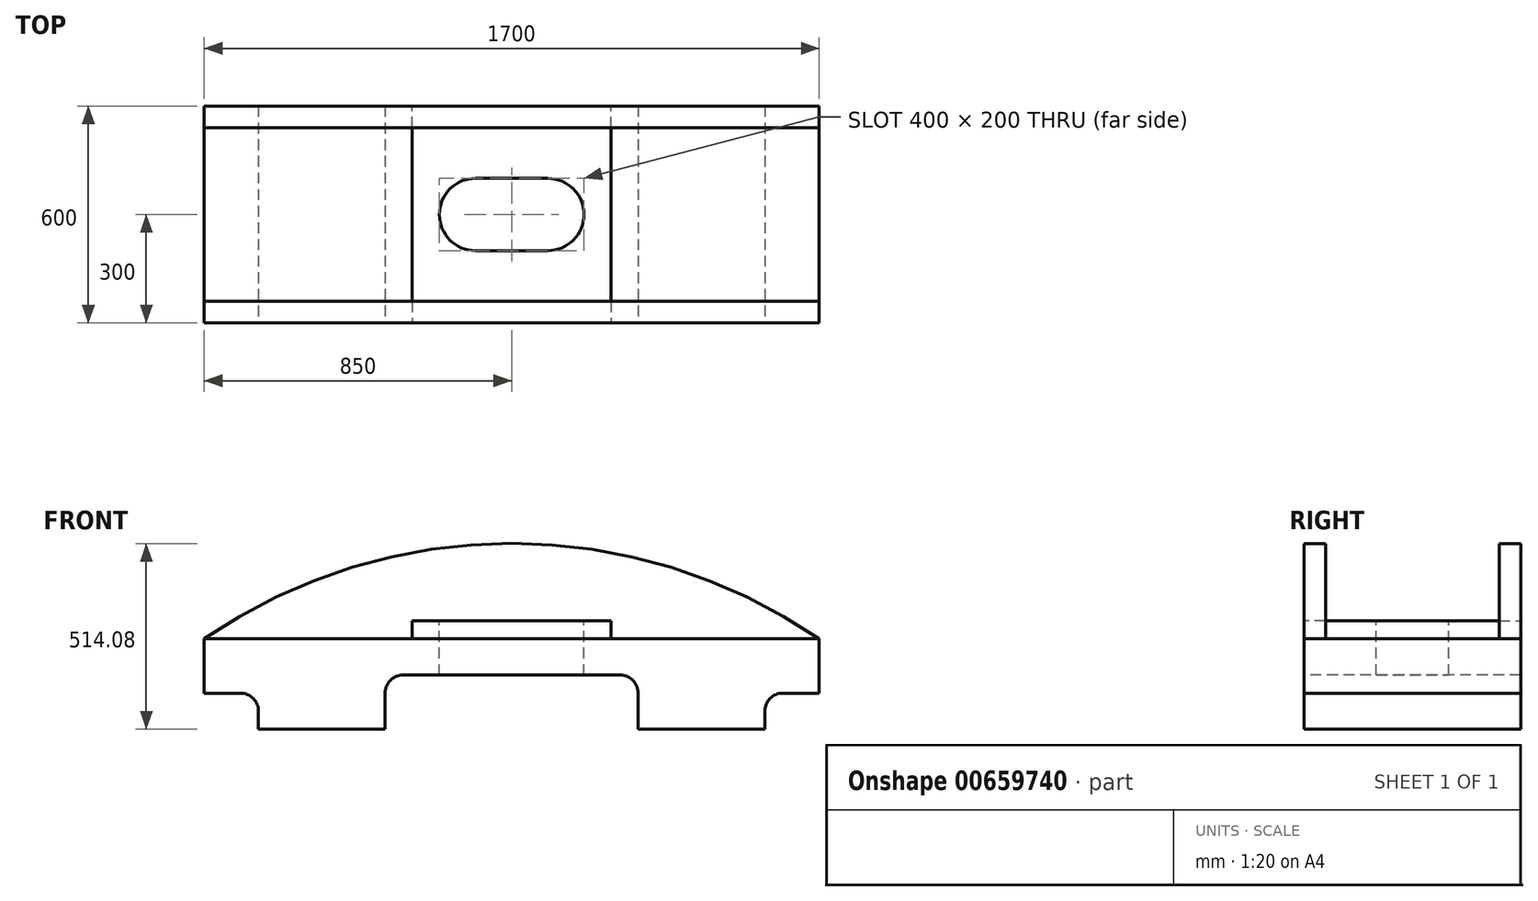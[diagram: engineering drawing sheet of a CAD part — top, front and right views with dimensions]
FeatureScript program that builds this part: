
annotation { "Feature Type Name" : "Feature", "Feature Type Description" : "" }
export const myFeature = defineFeature(function(context is Context, id is Id, definition is map)
    precondition{}
    {
        {
            var Q0;
            Q0=qCreatedBy(makeId("Front.planeOp"),FACE);
            var sketch = newSketch(context, id + "F0", { "sketchPlane" : qUnion([Q0])});
            skLineSegment(sketch, "E0.bottom", {"start": v(850, 125) * mm, "end": v(-850, 125) * mm});
            skLineSegment(sketch, "E0.top", {"start": v(850, -125) * mm, "end": v(-850, -125) * mm});
            skLineSegment(sketch, "E0.left", {"start": v(850, 125) * mm, "end": v(850, -125) * mm});
            skLineSegment(sketch, "E0.right", {"start": v(-850, 125) * mm, "end": v(-850, -125) * mm});
            skPoint(sketch, "E0.middle", {"position": v(0, 0) * mm});
            skSolve(sketch);
        }
        {
            var Q0;
            Q0 = qSketchRegion(id + "F0", true);
            extrude(context, id + "F1", {"entities" : qUnion([Q0]), "depth" : 600 * mm, "offsetDistance" : 25 * mm});
        }
        {
            var Q0;
            Q0=makeQuery(id+"F1.opExtrude","CAP_FACE",FACE,{"disambiguationData":[OSD([sQuery(id+"F0.wireOp",EDGE,"E0.bottom"),sQuery(id+"F0.wireOp",EDGE,"E0.top"),sQuery(id+"F0.wireOp",EDGE,"E0.left"),sQuery(id+"F0.wireOp",EDGE,"E0.right")])],"isStart":false});
            var sketch = newSketch(context, id + "F2", { "sketchPlane" : qUnion([Q0])});
            skPoint(sketch, "E1", {"position": v(-850, -25) * mm});
            skPoint(sketch, "E2", {"position": v(-700, -125) * mm});
            skPoint(sketch, "E3", {"position": v(850, -25) * mm});
            skPoint(sketch, "E4", {"position": v(700, -125) * mm});
            skLineSegment(sketch, "E5", {"start": v(-700, -75) * mm, "end": v(-700, -125) * mm});
            skLineSegment(sketch, "E6", {"start": v(-850, -25) * mm, "end": v(-750, -25) * mm});
            skPoint(sketch, "E7.visualSharp", {"position": v(-700, -25) * mm});
            skArc(sketch, "E7.filletArc", {"start": v(-700, -75) * mm, "mid": v(-714.64, -39.64) * mm, "end": v(-750, -25) * mm});
            skLineSegment(sketch, "E8", {"start": v(850, -25) * mm, "end": v(750, -25) * mm});
            skLineSegment(sketch, "E9", {"start": v(700, -75) * mm, "end": v(700, -125) * mm});
            skPoint(sketch, "E10.visualSharp", {"position": v(700, -25) * mm});
            skArc(sketch, "E10.filletArc", {"start": v(750, -25) * mm, "mid": v(714.64, -39.64) * mm, "end": v(700, -75) * mm});
            skLineSegment(sketch, "E11.bottom", {"start": v(300, 25) * mm, "end": v(-300, 25) * mm});
            skLineSegment(sketch, "E11.left", {"start": v(350, -25) * mm, "end": v(350, -125) * mm});
            skLineSegment(sketch, "E11.right", {"start": v(-350, -25) * mm, "end": v(-350, -125) * mm});
            skPoint(sketch, "E11.middle", {"position": v(0, -125) * mm});
            skLineSegment(sketch, "E12", {"start": v(-350, -125) * mm, "end": v(350, -125) * mm});
            skPoint(sketch, "E13.orphan", {"position": v(-350, -275) * mm});
            skPoint(sketch, "E14.orphan", {"position": v(350, -275) * mm});
            skPoint(sketch, "E15.visualSharp", {"position": v(-350, 25) * mm});
            skArc(sketch, "E15.filletArc", {"start": v(-300, 25) * mm, "mid": v(-335.36, 10.36) * mm, "end": v(-350, -25) * mm});
            skPoint(sketch, "E16.visualSharp", {"position": v(350, 25) * mm});
            skArc(sketch, "E16.filletArc", {"start": v(350, -25) * mm, "mid": v(335.36, 10.36) * mm, "end": v(300, 25) * mm});
            skSolve(sketch);
        }
        {
            var Q0;
            Q0 = qSketchRegion(id + "F2", true);
            var Q1;
            {var subQ3=sQuery(id+"F2.wireOp",EDGE,"E5");Q1=makeQuery(id+"F2.imprint","IMPRINT",FACE,{"disambiguationData":[TD([[makeQuery(id+"F2.imprint","IMPRINT",EDGE,{"derivedFrom":subQ3}),-1.0]])]});}
            var Q2;
            {var subQ4=sQuery(id+"F2.wireOp",EDGE,"E8");Q2=makeQuery(id+"F2.imprint","IMPRINT",FACE,{"disambiguationData":[TD([[makeQuery(id+"F2.imprint","IMPRINT",EDGE,{"derivedFrom":subQ4}),1.0]])]});}
            extrude(context, id + "F3", {"entities" : qUnion([Q0, Q1, Q2]), "operationType" : NewBodyOperationType.REMOVE, "endBound" : BoundingType.THROUGH_ALL, "oppositeDirection" : true, "depth" : 25 * mm, "offsetDistance" : 25 * mm});
        }
        {
            var Q0;
            Q0=makeQuery(id+"F1.opExtrude","CAP_FACE",FACE,{"disambiguationData":[OSD([sQuery(id+"F0.wireOp",EDGE,"E0.bottom"),sQuery(id+"F0.wireOp",EDGE,"E0.top"),sQuery(id+"F0.wireOp",EDGE,"E0.left"),sQuery(id+"F0.wireOp",EDGE,"E0.right")])],"isStart":false});
            var sketch = newSketch(context, id + "F4", { "sketchPlane" : qUnion([Q0])});
            skLineSegment(sketch, "E17.bottom", {"start": v(275, 175) * mm, "end": v(-275, 175) * mm});
            skLineSegment(sketch, "E17.left", {"start": v(275, 175) * mm, "end": v(275, 125) * mm});
            skLineSegment(sketch, "E17.right", {"start": v(-275, 175) * mm, "end": v(-275, 125) * mm});
            skPoint(sketch, "E17.middle", {"position": v(0, 125) * mm});
            skLineSegment(sketch, "E18", {"start": v(-275, 125) * mm, "end": v(275, 125) * mm});
            skPoint(sketch, "E19.orphan", {"position": v(-275, 75) * mm});
            skPoint(sketch, "E20.orphan", {"position": v(275, 75) * mm});
            skSolve(sketch);
        }
        {
            var Q0;
            Q0 = qSketchRegion(id + "F4", true);
            extrude(context, id + "F5", {"entities" : qUnion([Q0]), "operationType" : NewBodyOperationType.ADD, "oppositeDirection" : true, "depth" : 600 * mm, "offsetDistance" : 25 * mm});
        }
        {
            var Q0;
            Q0=makeQuery(id+"F5.opExtrude","SWEPT_FACE",FACE,{"disambiguationData":[OSD([sQuery(id+"F4.wireOp",EDGE,"E17.bottom")])]});
            var sketch = newSketch(context, id + "F6", { "sketchPlane" : qUnion([Q0])});
            skLineSegment(sketch, "E21.bottom", {"start": v(100, -200) * mm, "end": v(-100, -200) * mm});
            skLineSegment(sketch, "E21.top", {"start": v(100, -400) * mm, "end": v(-100, -400) * mm});
            skLineSegment(sketch, "E21.left", {"start": v(200, -300) * mm, "end": v(200, -300) * mm});
            skLineSegment(sketch, "E21.right", {"start": v(-200, -300) * mm, "end": v(-200, -300) * mm});
            skPoint(sketch, "E21.middle", {"position": v(0, -300) * mm});
            skPoint(sketch, "E21.middle.positionSnap0", {"position": v(275, -300) * mm});
            skPoint(sketch, "E21.centerSnap0", {"position": v(275, -300) * mm});
            skPoint(sketch, "E22.visualSharp", {"position": v(-200, -200) * mm});
            skArc(sketch, "E22.filletArc", {"start": v(-100, -200) * mm, "mid": v(-170.71, -229.29) * mm, "end": v(-200, -300) * mm});
            skPoint(sketch, "E23.visualSharp", {"position": v(-200, -400) * mm});
            skArc(sketch, "E23.filletArc", {"start": v(-200, -300) * mm, "mid": v(-170.71, -370.71) * mm, "end": v(-100, -400) * mm});
            skPoint(sketch, "E24.visualSharp", {"position": v(200, -400) * mm});
            skArc(sketch, "E24.filletArc", {"start": v(100, -400) * mm, "mid": v(170.71, -370.71) * mm, "end": v(200, -300) * mm});
            skPoint(sketch, "E25.visualSharp", {"position": v(200, -200) * mm});
            skArc(sketch, "E25.filletArc", {"start": v(200, -300) * mm, "mid": v(170.71, -229.29) * mm, "end": v(100, -200) * mm});
            skSolve(sketch);
        }
        {
            var Q0;
            Q0 = qSketchRegion(id + "F6", true);
            extrude(context, id + "F7", {"entities" : qUnion([Q0]), "operationType" : NewBodyOperationType.REMOVE, "endBound" : BoundingType.THROUGH_ALL, "oppositeDirection" : true, "depth" : 25 * mm, "offsetDistance" : 25 * mm});
        }
        {
            var Q0;
            Q0=makeQuery(id+"F5.boolean.opBoolean","MERGE",FACE,{"derivedFrom":[makeQuery(id+"F1.opExtrude","CAP_FACE",FACE,{"disambiguationData":[OSD([sQuery(id+"F0.wireOp",EDGE,"E0.bottom"),sQuery(id+"F0.wireOp",EDGE,"E0.top"),sQuery(id+"F0.wireOp",EDGE,"E0.left"),sQuery(id+"F0.wireOp",EDGE,"E0.right")])],"isStart":false}),makeQuery(id+"F5.opExtrude","CAP_FACE",FACE,{"disambiguationData":[OSD([sQuery(id+"F4.wireOp",EDGE,"E17.bottom"),sQuery(id+"F4.wireOp",EDGE,"E17.left"),sQuery(id+"F4.wireOp",EDGE,"E17.right"),sQuery(id+"F4.wireOp",EDGE,"E18")])],"isStart":true})]});
            var sketch = newSketch(context, id + "F8", { "sketchPlane" : qUnion([Q0])});
            skArc(sketch, "E26", {"start": v(850, 125) * mm, "mid": v(0, 389.08) * mm, "end": v(-850, 125) * mm});
            skLineSegment(sketch, "E27", {"start": v(-850, 125) * mm, "end": v(850, 125) * mm});
            skSolve(sketch);
        }
        {
            var Q0;
            Q0=makeQuery(id+"F8.imprint","IMPRINT",FACE,{"disambiguationData":[TD([[makeQuery(id+"F8.imprint","IMPRINT",EDGE,{"derivedFrom":makeQuery(id+"F5.opExtrude","CAP_EDGE",EDGE,{"disambiguationData":[OSD([sQuery(id+"F4.wireOp",EDGE,"E17.bottom")])],"isStart":true})}),1.0]])]});
            var Q1;
            {var subQ1=sQuery(id+"F8.wireOp",EDGE,"E26");Q1=makeQuery(id+"F8.imprint","IMPRINT",FACE,{"disambiguationData":[TD([[makeQuery(id+"F8.imprint","IMPRINT",EDGE,{"derivedFrom":subQ1}),1.0]])]});}
            var Q2;
            Q2=sQuery(id+"F8.wireOp",EDGE,"E26");
            extrude(context, id + "F9", {"entities" : qUnion([Q0, Q1]), "surfaceEntities" : qUnion([Q2]), "oppositeDirection" : true, "depth" : 60 * mm, "offsetDistance" : 25 * mm});
        }
        {
            var Q0;
            Q0=makeQuery(id+"F5.boolean.opBoolean","MERGE",FACE,{"derivedFrom":[makeQuery(id+"F1.opExtrude","CAP_FACE",FACE,{"disambiguationData":[OSD([sQuery(id+"F0.wireOp",EDGE,"E0.bottom"),sQuery(id+"F0.wireOp",EDGE,"E0.top"),sQuery(id+"F0.wireOp",EDGE,"E0.left"),sQuery(id+"F0.wireOp",EDGE,"E0.right")])],"isStart":true}),makeQuery(id+"F5.opExtrude","CAP_FACE",FACE,{"disambiguationData":[OSD([sQuery(id+"F4.wireOp",EDGE,"E17.bottom"),sQuery(id+"F4.wireOp",EDGE,"E17.left"),sQuery(id+"F4.wireOp",EDGE,"E17.right"),sQuery(id+"F4.wireOp",EDGE,"E18")])],"isStart":false})]});
            var sketch = newSketch(context, id + "F10", { "sketchPlane" : qUnion([Q0])});
            skArc(sketch, "E28", {"start": v(850, 125) * mm, "mid": v(0, 389.08) * mm, "end": v(-850, 125) * mm});
            skSolve(sketch);
        }
        {
            var Q0;
            Q0 = qSketchRegion(id + "F10", true);
            var Q1;
            Q1=makeQuery(id+"F10.imprint","IMPRINT",FACE,{"disambiguationData":[TD([[makeQuery(id+"F10.imprint","IMPRINT",EDGE,{"derivedFrom":sQuery(id+"F10.wireOp",EDGE,"E28")}),1.0]])]});
            extrude(context, id + "F11", {"entities" : qUnion([Q0, Q1]), "oppositeDirection" : true, "depth" : 60 * mm, "offsetDistance" : 25 * mm});
        }
    });
